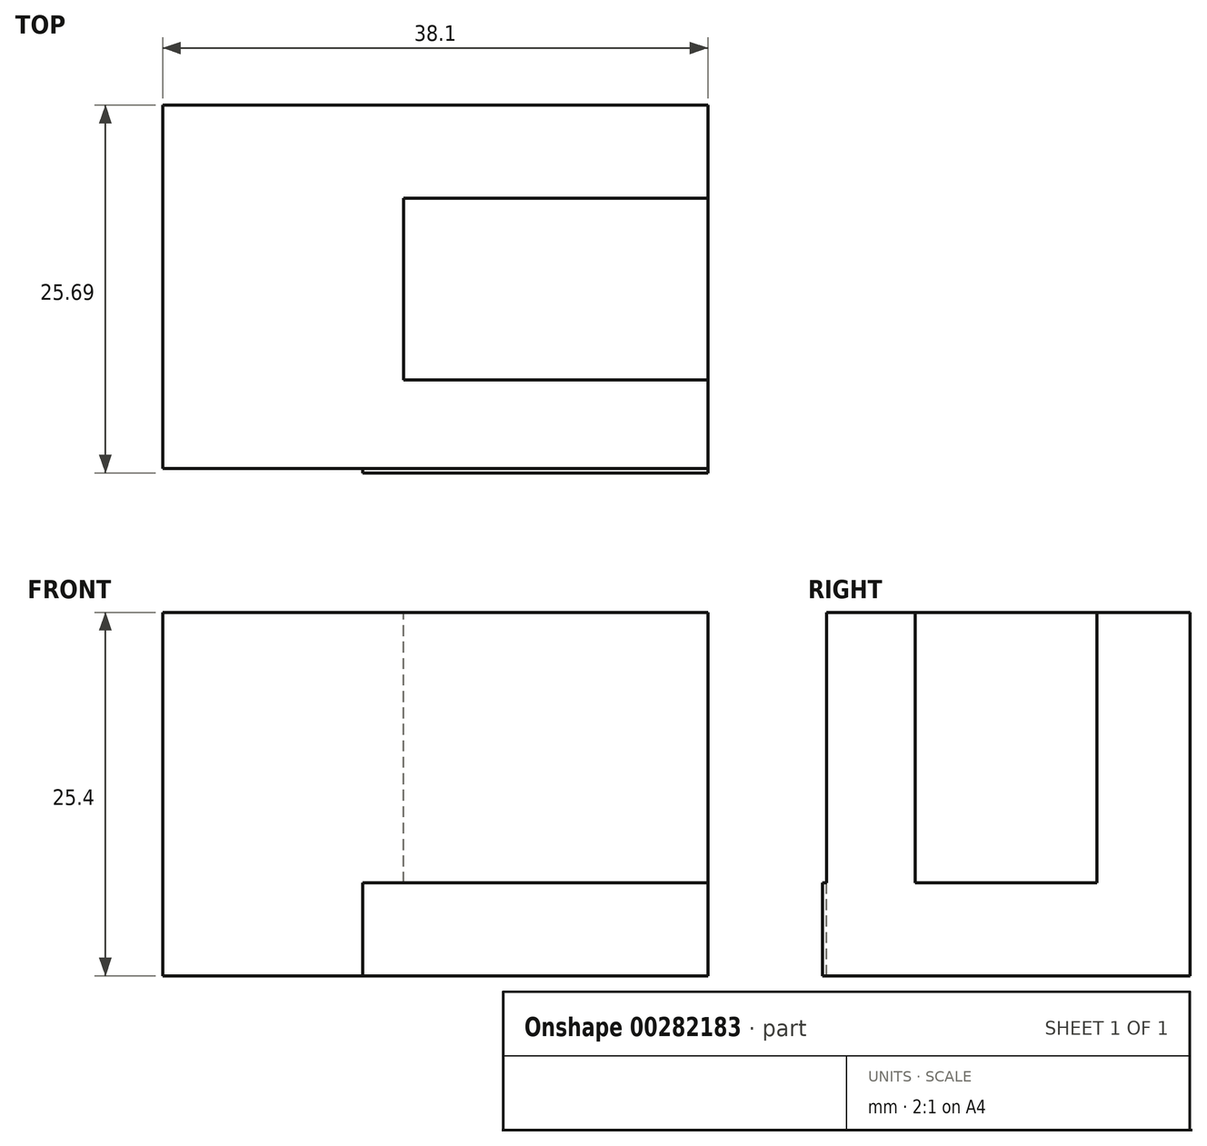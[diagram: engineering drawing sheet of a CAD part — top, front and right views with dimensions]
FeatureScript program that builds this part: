
annotation { "Feature Type Name" : "Feature", "Feature Type Description" : "" }
export const myFeature = defineFeature(function(context is Context, id is Id, definition is map)
    precondition{}
    {
        {
            var Q0;
            Q0=qCreatedBy(makeId("Front.planeOp"),FACE);
            var sketch = newSketch(context, id + "F0", { "sketchPlane" : qUnion([Q0])});
            skLineSegment(sketch, "E0.bottom", {"start": v(0, 0) * mm, "end": v(38.1, 0) * mm});
            skLineSegment(sketch, "E0.top", {"start": v(0, 25.4) * mm, "end": v(38.1, 25.4) * mm});
            skLineSegment(sketch, "E0.left", {"start": v(0, 0) * mm, "end": v(0, 25.4) * mm});
            skLineSegment(sketch, "E0.right", {"start": v(38.1, 0) * mm, "end": v(38.1, 25.4) * mm});
            skSolve(sketch);
        }
        {
            var Q0;
            Q0 = qSketchRegion(id + "F0", true);
            extrude(context, id + "F1", {"entities" : qUnion([Q0]), "endBound" : BoundingType.SYMMETRIC, "depth" : 25.4 * mm});
        }
        {
            var Q0;
            Q0=makeQuery(id+"F1.opExtrude","SWEPT_FACE",FACE,{"disambiguationData":[OSD([sQuery(id+"F0.wireOp",EDGE,"E0.top")])]});
            var sketch = newSketch(context, id + "F2", { "sketchPlane" : qUnion([Q0])});
            skLineSegment(sketch, "E1.bottom", {"start": v(38.1, 6.2) * mm, "end": v(16.83, 6.2) * mm});
            skLineSegment(sketch, "E1.top", {"start": v(38.1, -6.5) * mm, "end": v(16.83, -6.5) * mm});
            skLineSegment(sketch, "E1.left", {"start": v(38.1, 6.2) * mm, "end": v(38.1, -6.5) * mm});
            skLineSegment(sketch, "E1.right", {"start": v(16.83, 6.2) * mm, "end": v(16.83, -6.5) * mm});
            skLineSegment(sketch, "E2.bottom", {"start": v(38.1, -6.5) * mm, "end": v(38.1, -6.5) * mm});
            skLineSegment(sketch, "E2.top", {"start": v(38.1, 6.2) * mm, "end": v(38.1, 6.2) * mm});
            skLineSegment(sketch, "E2.left", {"start": v(38.1, -6.5) * mm, "end": v(38.1, 6.2) * mm});
            skLineSegment(sketch, "E2.right", {"start": v(38.1, -6.5) * mm, "end": v(38.1, 6.2) * mm});
            skSolve(sketch);
        }
        {
            var Q0;
            Q0 = qSketchRegion(id + "F2", true);
            extrude(context, id + "F3", {"entities" : qUnion([Q0]), "operationType" : NewBodyOperationType.REMOVE, "oppositeDirection" : true, "depth" : 25.4 * mm});
        }
        {
            var Q0;
            {var subQ1=sQuery(id+"F0.wireOp",EDGE,"E0.right");Q0=makeQuery(id+"F3.boolean.opBoolean","SPLIT",FACE,{"disambiguationData":[TD([makeQuery(id+"F3.opExtrude","SWEPT_FACE",FACE,{"disambiguationData":[OSD([sQuery(id+"F2.wireOp",EDGE,"E1.bottom")])]})])],"derivedFrom":makeQuery(id+"F1.opExtrude","SWEPT_FACE",FACE,{"disambiguationData":[OSD([subQ1])]})});}
            var sketch = newSketch(context, id + "F4", { "sketchPlane" : qUnion([Q0])});
            skLineSegment(sketch, "E3.bottom", {"start": v(-13, 0) * mm, "end": v(12.7, 0) * mm});
            skLineSegment(sketch, "E3.top", {"start": v(-13, 6.5) * mm, "end": v(12.7, 6.5) * mm});
            skLineSegment(sketch, "E3.left", {"start": v(-13, 0) * mm, "end": v(-13, 6.5) * mm});
            skLineSegment(sketch, "E3.right", {"start": v(12.7, 0) * mm, "end": v(12.7, 6.5) * mm});
            skSolve(sketch);
        }
        {
            var Q0;
            Q0 = qSketchRegion(id + "F4", true);
            extrude(context, id + "F5", {"entities" : qUnion([Q0]), "operationType" : NewBodyOperationType.ADD, "oppositeDirection" : true, "depth" : 24.13 * mm});
        }
    });
